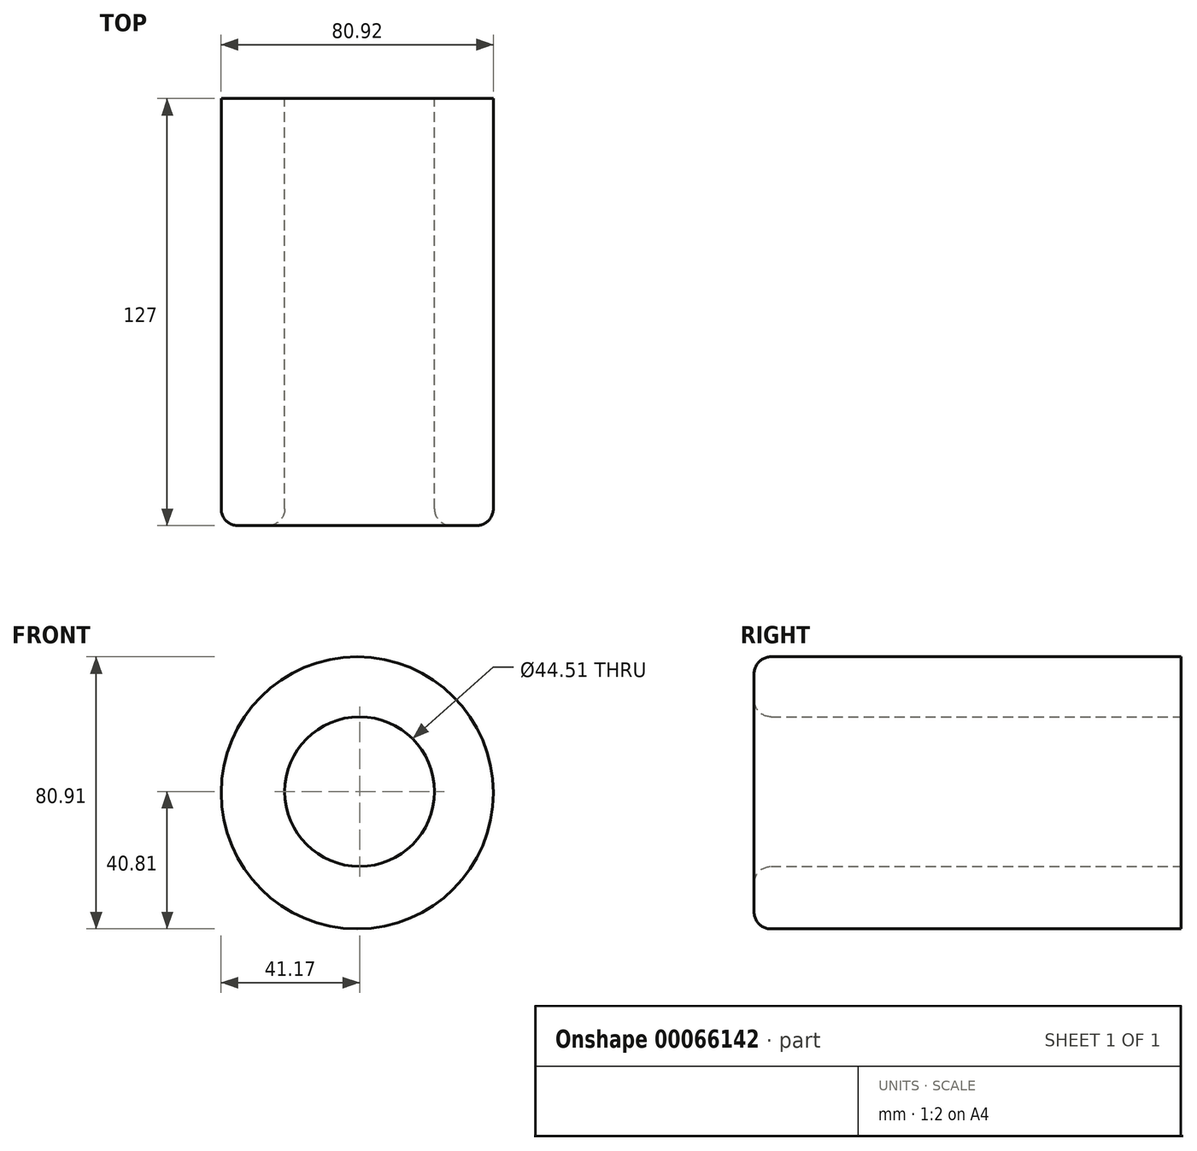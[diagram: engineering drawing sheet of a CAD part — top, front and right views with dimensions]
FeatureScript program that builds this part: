
annotation { "Feature Type Name" : "Feature", "Feature Type Description" : "" }
export const myFeature = defineFeature(function(context is Context, id is Id, definition is map)
    precondition{}
    {
        {
            var Q0;
            Q0=qCreatedBy(makeId("Front.planeOp"),FACE);
            var sketch = newSketch(context, id + "F0", { "sketchPlane" : qUnion([Q0])});
            skCircle(sketch, "E0", {"center": v(0, 0) * mm, "radius": 22.25 * mm});
            skCircle(sketch, "E1", {"center": v(-0.7, -0.36) * mm, "radius": 40.46 * mm});
            skPoint(sketch, "E1.first.point", {"position": v(-26.98, -31.12) * mm});
            skPoint(sketch, "E1.second.point", {"position": v(-26.45, 30.86) * mm});
            skPoint(sketch, "E1.third.point", {"position": v(37.4, 13.22) * mm});
            skSolve(sketch);
        }
        {
            var Q0;
            Q0 = qSketchRegion(id + "F0", true);
            extrude(context, id + "F1", {"entities" : qUnion([Q0]), "depth" : 127 * mm});
        }
        {
            var Q0;
            Q0 = qSketchRegion(id + "F0", true);
            extrude(context, id + "F2", {"entities" : qUnion([Q0]), "operationType" : NewBodyOperationType.ADD, "depth" : 50 * mm});
        }
        {
            var Q0;
            Q0=makeQuery(id+"F1.opExtrude","CAP_EDGE",EDGE,{"disambiguationData":[OSD([sQuery(id+"F0.wireOp",EDGE,"E1")])],"isStart":false});
            fillet(context, id + "F3", {"entities" : qUnion([Q0]), "radius" : 5 * mm, "tangentPropagation" : true, "allowEdgeOverflow" : false});
        }
        {
            var Q0;
            Q0=makeQuery(id+"F1.opExtrude","CAP_EDGE",EDGE,{"disambiguationData":[OSD([sQuery(id+"F0.wireOp",EDGE,"E0")])],"isStart":false});
            fillet(context, id + "F4", {"entities" : qUnion([Q0]), "radius" : 5 * mm, "tangentPropagation" : true, "allowEdgeOverflow" : false});
        }
    });
